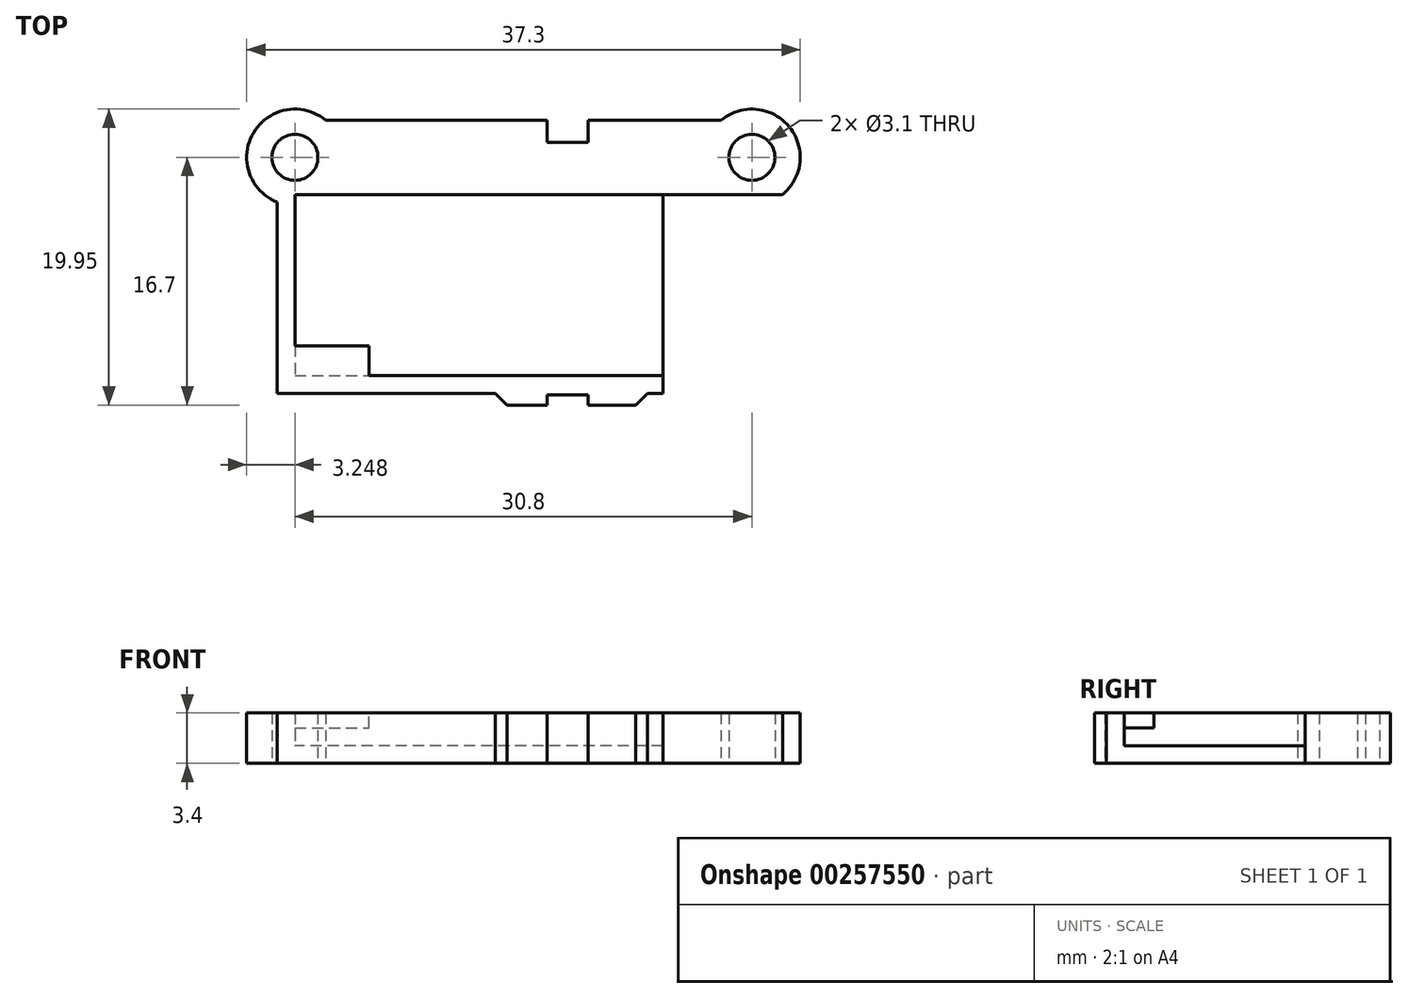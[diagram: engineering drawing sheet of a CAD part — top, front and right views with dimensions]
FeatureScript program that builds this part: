
annotation { "Feature Type Name" : "Feature", "Feature Type Description" : "" }
export const myFeature = defineFeature(function(context is Context, id is Id, definition is map)
    precondition{}
    {
        {
            var Q0;
            Q0=qCreatedBy(makeId("Top.planeOp"),FACE);
            var sketch = newSketch(context, id + "F0", { "sketchPlane" : qUnion([Q0])});
            skCircle(sketch, "E0", {"center": v(-15.23, 0) * mm, "radius": 1.55 * mm});
            skCircle(sketch, "E1", {"center": v(15.57, 0) * mm, "radius": 1.55 * mm});
            skCircle(sketch, "E2", {"center": v(-15.23, 0) * mm, "radius": 3.25 * mm});
            skCircle(sketch, "E3", {"center": v(15.57, 0) * mm, "radius": 3.25 * mm});
            skLineSegment(sketch, "E4", {"start": v(-11.73, -2.5) * mm, "end": v(9.57, -2.5) * mm});
            skLineSegment(sketch, "E5", {"start": v(-13.16, 2.5) * mm, "end": v(13.5, 2.5) * mm});
            skLineSegment(sketch, "E6", {"start": v(-11.73, -2.5) * mm, "end": v(-11.73, -15.9) * mm});
            skLineSegment(sketch, "E7", {"start": v(-11.73, -15.9) * mm, "end": v(9.57, -15.9) * mm});
            skLineSegment(sketch, "E8", {"start": v(9.57, -15.9) * mm, "end": v(9.57, -2.5) * mm});
            skLineSegment(sketch, "E9", {"start": v(-11.73, -14.7) * mm, "end": v(9.57, -14.7) * mm});
            skLineSegment(sketch, "E10", {"start": v(-11.73, -2.5) * mm, "end": v(-11.73, 0) * mm});
            skLineSegment(sketch, "E11", {"start": v(9.57, -2.5) * mm, "end": v(9.57, 0) * mm});
            skLineSegment(sketch, "E12", {"start": v(9.57, 0) * mm, "end": v(-11.73, 0) * mm});
            skLineSegment(sketch, "E13", {"start": v(-11.73, 0) * mm, "end": v(-11.98, 0) * mm});
            skLineSegment(sketch, "E14", {"start": v(-15.23, -15.9) * mm, "end": v(-11.73, -15.9) * mm});
            skLineSegment(sketch, "E15", {"start": v(-15.23, 0) * mm, "end": v(-15.23, -15.9) * mm});
            skLineSegment(sketch, "E16", {"start": v(-16.43, -15.9) * mm, "end": v(-16.43, -0.98) * mm});
            skLineSegment(sketch, "E17", {"start": v(-15.23, -15.9) * mm, "end": v(-16.43, -15.9) * mm});
            skLineSegment(sketch, "E18", {"start": v(-11.73, -14.7) * mm, "end": v(-16.43, -14.7) * mm});
            skLineSegment(sketch, "E19", {"start": v(-11.73, -2.5) * mm, "end": v(-16.43, -2.5) * mm});
            skLineSegment(sketch, "E20", {"start": v(9.57, -2.5) * mm, "end": v(17.64, -2.5) * mm});
            skLineSegment(sketch, "E21", {"start": v(1.77, 2.5) * mm, "end": v(1.77, 1) * mm});
            skLineSegment(sketch, "E22", {"start": v(1.77, 1) * mm, "end": v(4.52, 1) * mm});
            skLineSegment(sketch, "E23", {"start": v(4.52, 1) * mm, "end": v(4.52, 2.5) * mm});
            skLineSegment(sketch, "E24", {"start": v(4.52, -16.7) * mm, "end": v(-0.23, -16.7) * mm});
            skLineSegment(sketch, "E25", {"start": v(-0.23, -16.7) * mm, "end": v(-0.23, -15.9) * mm});
            skLineSegment(sketch, "E26", {"start": v(1.77, -16.7) * mm, "end": v(1.77, -16) * mm});
            skLineSegment(sketch, "E27", {"start": v(1.77, -16) * mm, "end": v(4.52, -16) * mm});
            skLineSegment(sketch, "E28", {"start": v(4.52, -16) * mm, "end": v(4.52, -16.7) * mm});
            skLineSegment(sketch, "E29", {"start": v(4.52, -16.7) * mm, "end": v(7.02, -16.7) * mm});
            skLineSegment(sketch, "E30", {"start": v(7.02, -16.7) * mm, "end": v(7.02, -15.9) * mm});
            skSolve(sketch);
        }
        {
            var Q0;
            {var subQ5=sQuery(id+"F0.wireOp",EDGE,"E16");var subQ8=sQuery(id+"F0.wireOp",EDGE,"E0");var subQ9=makeQuery(id+"F0.imprint","INTERSECT",VERTEX,{"derivedFrom":[subQ8,subQ5]});Q0=makeQuery(id+"F0.imprint","IMPRINT",FACE,{"disambiguationData":[TD([[makeQuery(id+"F0.imprint","IMPRINT",EDGE,{"disambiguationData":[TD([[subQ9,1.0]])],"derivedFrom":subQ8}),-1.0]])]});}
            var Q1;
            {var subQ0=sQuery(id+"F0.wireOp",EDGE,"E16");var subQ1=sQuery(id+"F0.wireOp",EDGE,"E0");var subQ2=makeQuery(id+"F0.imprint","INTERSECT",VERTEX,{"derivedFrom":[subQ1,subQ0]});Q1=makeQuery(id+"F0.imprint","IMPRINT",FACE,{"disambiguationData":[TD([[makeQuery(id+"F0.imprint","IMPRINT",EDGE,{"disambiguationData":[TD([[subQ2,-1.0]])],"derivedFrom":subQ1}),-1.0]])]});}
            var Q2;
            {var subQ4=sQuery(id+"F0.wireOp",EDGE,"E10");Q2=makeQuery(id+"F0.imprint","IMPRINT",FACE,{"disambiguationData":[TD([[makeQuery(id+"F0.imprint","IMPRINT",EDGE,{"derivedFrom":subQ4}),1.0]])]});}
            var Q3;
            {var subQ1=sQuery(id+"F0.wireOp",EDGE,"E5");Q3=makeQuery(id+"F0.imprint","IMPRINT",FACE,{"disambiguationData":[TD([[makeQuery(id+"F0.imprint","IMPRINT",EDGE,{"derivedFrom":subQ1}),-1.0]])]});}
            var Q4;
            Q4=makeQuery(id+"F0.imprint","IMPRINT",FACE,{"disambiguationData":[TD([[makeQuery(id+"F0.imprint","IMPRINT",EDGE,{"derivedFrom":sQuery(id+"F0.wireOp",EDGE,"E4")}),1.0]])]});
            var Q5;
            Q5=makeQuery(id+"F0.imprint","IMPRINT",FACE,{"disambiguationData":[TD([[makeQuery(id+"F0.imprint","IMPRINT",EDGE,{"derivedFrom":sQuery(id+"F0.wireOp",EDGE,"E1")}),-1.0]])]});
            extrude(context, id + "F1", {"entities" : qUnion([Q0, Q1, Q2, Q3, Q4, Q5]), "depth" : 3.4 * mm});
        }
        {
            var Q0;
            {var subQ0=sQuery(id+"F0.wireOp",EDGE,"E16");var subQ1=sQuery(id+"F0.wireOp",EDGE,"E2");var subQ2=makeQuery(id+"F0.imprint","INTERSECT",VERTEX,{"derivedFrom":[subQ1,subQ0]});Q0=makeQuery(id+"F0.imprint","IMPRINT",FACE,{"disambiguationData":[TD([[makeQuery(id+"F0.imprint","IMPRINT",EDGE,{"disambiguationData":[TD([[subQ2,-1.0]])],"derivedFrom":subQ1}),-1.0]])]});}
            var Q1;
            {var subQ0=sQuery(id+"F0.wireOp",EDGE,"E16");var subQ1=sQuery(id+"F0.wireOp",EDGE,"E2");var subQ2=makeQuery(id+"F0.imprint","INTERSECT",VERTEX,{"derivedFrom":[subQ1,subQ0]});Q1=makeQuery(id+"F0.imprint","IMPRINT",FACE,{"disambiguationData":[TD([[makeQuery(id+"F0.imprint","IMPRINT",EDGE,{"disambiguationData":[TD([[subQ2,-1.0]])],"derivedFrom":subQ1}),1.0]])]});}
            var Q2;
            {var subQ0=sQuery(id+"F0.wireOp",EDGE,"E17");Q2=makeQuery(id+"F0.imprint","IMPRINT",FACE,{"disambiguationData":[TD([[makeQuery(id+"F0.imprint","IMPRINT",EDGE,{"derivedFrom":subQ0}),-1.0]])]});}
            var Q3;
            {var subQ0=sQuery(id+"F0.wireOp",EDGE,"E14");Q3=makeQuery(id+"F0.imprint","IMPRINT",FACE,{"disambiguationData":[TD([[makeQuery(id+"F0.imprint","IMPRINT",EDGE,{"derivedFrom":subQ0}),1.0]])]});}
            var Q4;
            {var subQ0=sQuery(id+"F0.wireOp",EDGE,"E7");Q4=makeQuery(id+"F0.imprint","IMPRINT",FACE,{"disambiguationData":[TD([[makeQuery(id+"F0.imprint","IMPRINT",EDGE,{"derivedFrom":subQ0}),1.0]])]});}
            var Q5;
            {var subQ3=sQuery(id+"F0.wireOp",EDGE,"xuWslP24-Mjdm-qhvh-AI0n-hdlMBYz60Hd2");Q5=makeQuery(id+"F0.imprint","IMPRINT",FACE,{"disambiguationData":[TD([[makeQuery(id+"F0.imprint","IMPRINT",EDGE,{"derivedFrom":subQ3}),-1.0]])]});}
            var Q6;
            {var subQ1=sQuery(id+"F0.wireOp",EDGE,"E25");Q6=makeQuery(id+"F0.imprint","IMPRINT",FACE,{"disambiguationData":[TD([[makeQuery(id+"F0.imprint","IMPRINT",EDGE,{"derivedFrom":subQ1}),-1.0]])]});}
            extrude(context, id + "F2", {"entities" : qUnion([Q0, Q1, Q2, Q3, Q4, Q5, Q6]), "operationType" : NewBodyOperationType.ADD, "depth" : 3.4 * mm});
        }
        {
            var Q0;
            {var subQ3=sQuery(id+"F0.wireOp",EDGE,"E15");var subQ5=sQuery(id+"F0.wireOp",EDGE,"E2");var subQ6=makeQuery(id+"F0.imprint","INTERSECT",VERTEX,{"derivedFrom":[subQ5,subQ3]});Q0=makeQuery(id+"F0.imprint","IMPRINT",FACE,{"disambiguationData":[TD([[makeQuery(id+"F0.imprint","IMPRINT",EDGE,{"disambiguationData":[TD([[subQ6,-1.0]])],"derivedFrom":subQ5}),-1.0]])]});}
            var Q1;
            {var subQ0=sQuery(id+"F0.wireOp",EDGE,"E15");var subQ1=sQuery(id+"F0.wireOp",EDGE,"E2");var subQ2=makeQuery(id+"F0.imprint","INTERSECT",VERTEX,{"derivedFrom":[subQ1,subQ0]});Q1=makeQuery(id+"F0.imprint","IMPRINT",FACE,{"disambiguationData":[TD([[makeQuery(id+"F0.imprint","IMPRINT",EDGE,{"disambiguationData":[TD([[subQ2,-1.0]])],"derivedFrom":subQ1}),1.0]])]});}
            var Q2;
            {var subQ0=sQuery(id+"F0.wireOp",EDGE,"E4");Q2=makeQuery(id+"F0.imprint","IMPRINT",FACE,{"disambiguationData":[TD([[makeQuery(id+"F0.imprint","IMPRINT",EDGE,{"derivedFrom":subQ0}),-1.0]])]});}
            extrude(context, id + "F3", {"entities" : qUnion([Q0, Q1, Q2]), "operationType" : NewBodyOperationType.ADD, "depth" : 1.2 * mm});
        }
        {
            var Q0;
            Q0=makeQuery(id+"F2.opExtrude","SWEPT_FACE",FACE,{"disambiguationData":[OSD([sQuery(id+"F0.wireOp",EDGE,"E9"),sQuery(id+"F0.wireOp",EDGE,"E18")])]});
            var sketch = newSketch(context, id + "F4", { "sketchPlane" : qUnion([Q0])});
            skLineSegment(sketch, "E31", {"start": v(15.23, 2.4) * mm, "end": v(10.23, 2.4) * mm});
            skLineSegment(sketch, "E32", {"start": v(10.23, 2.4) * mm, "end": v(10.23, 3.4) * mm});
            skSolve(sketch);
        }
        {
            var Q0;
            {var subQ0=sQuery(id+"F4.wireOp",EDGE,"E31");Q0=makeQuery(id+"F4.imprint","IMPRINT",FACE,{"disambiguationData":[TD([[makeQuery(id+"F4.imprint","IMPRINT",EDGE,{"derivedFrom":subQ0}),-1.0]])]});}
            extrude(context, id + "F5", {"entities" : qUnion([Q0]), "operationType" : NewBodyOperationType.ADD, "depth" : 2 * mm});
        }
        {
            var Q0;
            Q0=makeQuery(id+"F2.opExtrude","SWEPT_EDGE",EDGE,{"disambiguationData":[OSD([sQuery(id+"F0.wireOp",EDGE,"E7"),sQuery(id+"F0.wireOp",EDGE,"E25")])]});
            var Q1;
            Q1=makeQuery(id+"F2.opExtrude","SWEPT_EDGE",EDGE,{"disambiguationData":[OSD([sQuery(id+"F0.wireOp",EDGE,"E7"),sQuery(id+"F0.wireOp",EDGE,"E30")])]});
            chamfer(context, id + "F6", {"entities" : qUnion([Q0, Q1]), "width" : 1.5 * mm, "tangentPropagation" : true});
        }
    });
